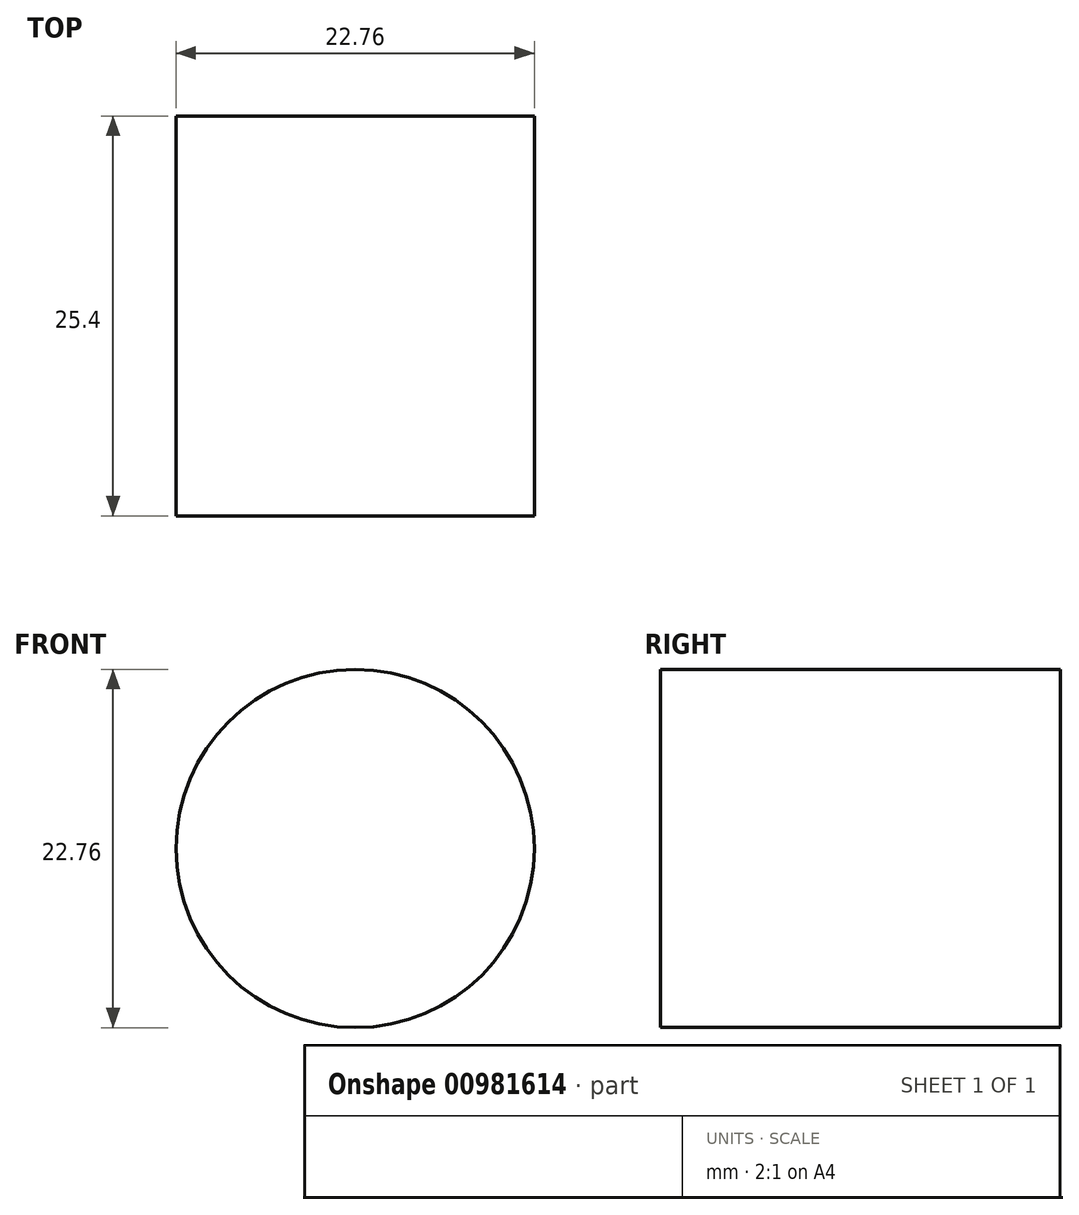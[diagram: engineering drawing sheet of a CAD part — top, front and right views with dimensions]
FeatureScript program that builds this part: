
annotation { "Feature Type Name" : "Feature", "Feature Type Description" : "" }
export const myFeature = defineFeature(function(context is Context, id is Id, definition is map)
    precondition{}
    {
        {
            var Q0;
            Q0=qCreatedBy(makeId("Front.planeOp"),FACE);
            var sketch = newSketch(context, id + "F0", { "sketchPlane" : qUnion([Q0])});
            skCircle(sketch, "E0", {"center": v(0, 0) * mm, "radius": 11.38 * mm});
            skSolve(sketch);
        }
        {
            var Q0;
            Q0 = qSketchRegion(id + "F0", true);
            extrude(context, id + "F1", {"entities" : qUnion([Q0]), "depth" : 25.4 * mm, "offsetDistance" : 25.4 * mm});
        }
    });
